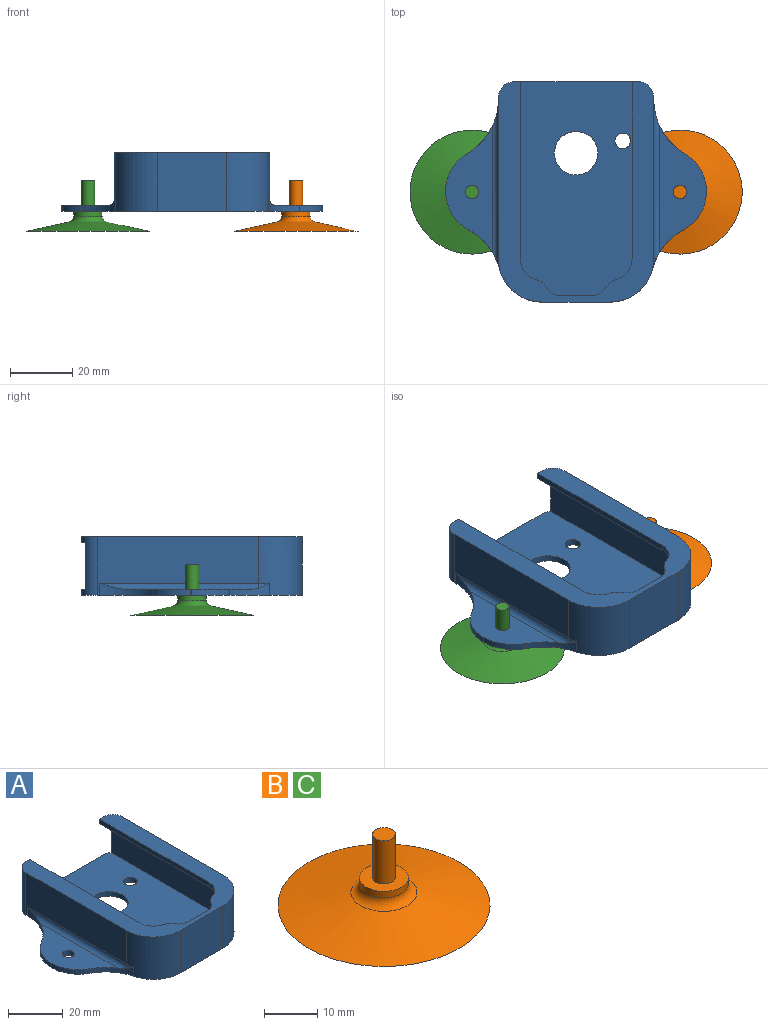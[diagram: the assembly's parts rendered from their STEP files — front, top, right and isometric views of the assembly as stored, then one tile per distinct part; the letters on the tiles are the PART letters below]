
ASSEMBLY  parts=3 mates=2
PART A: 48 faces, bbox 84.1x71x19 mm
  f0: plane 52x19mm, normal (-1,0,0), area 782.9mm2, adj f8,f9,f22,f27,f40,f43
  f1: plane 52x19mm, normal (1,0,0), area 782.9mm2, adj f8,f10,f22,f28,f33,f45
  f2: plane 40.1x2mm, normal (0,1,0), area 80.2mm2, adj f8,f14,f27,f28
  f3: plane 2x2mm, normal (0,1,0), area 4mm2, adj f5,f18,f22,f28
  f4: plane 69x18.01mm, normal (0,0,-1), area 367.1mm2, adj f6,f11,f12,f15,f20,f21,f23,f25
  f5: plane 69x18.01mm, normal (0,0,-1), area 367.1mm2, adj f3,f12,f13,f16,f18,f19,f24,f26
  f6: plane 2x2mm, normal (0,1,0), area 4mm2, adj f4,f21,f22,f27
  f7: plane 22.1x19mm, normal (0,-1,0), area 419.9mm2, adj f8,f9,f10,f22
  f8: plane 84.1x71mm, normal (0,0,-1), area 4177.7mm2, adj f0,f1,f2,f7,f9,f10,f17,f27
  f9: cylinder r=14mm len=19mm, axis (0,0,-1), area 403.8mm2, adj f0,f7,f8,f22,f39,f44
  f10: cylinder r=14mm len=19mm, axis (0,0,1), area 403.8mm2, adj f1,f7,f8,f22,f32,f46
  f11: plane 56x15mm, normal (1,0,0), area 840mm2, adj f4,f14,f15,f27
  f12: plane 22.1x17mm, normal (0,1,0), area 351.7mm2, adj f4,f5,f14,f15,f16,f22,f23,f24
  f13: plane 56x15mm, normal (-1,0,0), area 840mm2, adj f5,f14,f16,f28
  f14: plane 69x46.1mm, normal (0,0,1), area 2943.6mm2, adj f2,f11,f12,f13,f15,f16,f17,f27
  f15: cylinder r=12mm len=15mm, axis (0,0,-1), area 282.7mm2, adj f4,f11,f12,f14
  f16: cylinder r=12mm len=15mm, axis (0,0,1), area 282.7mm2, adj f5,f12,f13,f14
  f17: cylinder r=7mm len=14mm, axis (0,0,1), area 88mm2, adj f8,f14
  f18: plane 57x2mm, normal (-1,0,0), area 114mm2, adj f3,f5,f19,f22
  f19: cylinder r=7mm len=6.68mm, axis (0,0,-1), area 17.8mm2, adj f5,f18,f22,f26
  f20: cylinder r=7mm len=6.68mm, axis (0,0,-1), area 17.8mm2, adj f4,f21,f22,f25
  f21: plane 57x2mm, normal (1,0,0), area 114mm2, adj f4,f6,f20,f22
  f22: plane 71x50.1mm, normal (0,0,1), area 1079.3mm2, adj f0,f1,f3,f6,f7,f9,f10,f12
  f23: cylinder r=5mm len=4.24mm, axis (0,0,1), area 10.1mm2, adj f4,f12,f22,f25
  f24: cylinder r=5mm len=4.24mm, axis (0,0,1), area 10.1mm2, adj f5,f12,f22,f26
  f25: cylinder r=7mm len=3.85mm, axis (0,0,1), area 9.9mm2, adj f4,f20,f22,f23
  f26: cylinder r=7mm len=3.85mm, axis (0,0,1), area 9.9mm2, adj f5,f19,f22,f24
  f27: cylinder r=5mm len=19mm, axis (0,0,1), area 101mm2, adj f0,f2,f4,f6,f8,f11,f14,f22
  f28: cylinder r=5mm len=19mm, axis (0,0,-1), area 101mm2, adj f1,f2,f3,f5,f8,f13,f14,f22
  f29: plane 2x0.2mm, normal (1,0,0), area 0.4mm2, adj f8,f30,f34,f35
  f30: plane 40.34x15mm, normal (0,0,1), area 354.2mm2, adj f29,f31,f32,f33,f34,f35,f45
  f31: cylinder r=2.15mm len=4.3mm, axis (0,0,1), area 27mm2, adj f8,f30
  f32: cylinder r=20mm len=12.72mm, axis (0,0,1), area 38.1mm2, adj f8,f10,f30,f35,f45,f46
  f33: cylinder r=20mm len=17.32mm, axis (0,0,1), area 48.9mm2, adj f1,f8,f30,f34,f45
  f34: cylinder r=14mm len=12.12mm, axis (0,0,1), area 29.3mm2, adj f8,f29,f30,f33
  f35: cylinder r=14mm len=12.37mm, axis (0,0,1), area 30.3mm2, adj f8,f29,f30,f32
  f36: plane 2x0.2mm, normal (-1,0,0), area 0.4mm2, adj f8,f37,f41,f42
  f37: plane 40.34x15mm, normal (0,0,1), area 354.2mm2, adj f36,f38,f39,f40,f41,f42,f43
  f38: cylinder r=2.15mm len=4.3mm, axis (0,0,1), area 27mm2, adj f8,f37
  f39: cylinder r=20mm len=12.72mm, axis (0,0,1), area 38.1mm2, adj f8,f9,f37,f42,f43,f44
  f40: cylinder r=20mm len=17.32mm, axis (0,0,1), area 48.9mm2, adj f0,f8,f37,f41,f43
  f41: cylinder r=14mm len=12.12mm, axis (0,0,1), area 29.3mm2, adj f8,f36,f37,f40
  f42: cylinder r=14mm len=12.37mm, axis (0,0,1), area 30.3mm2, adj f8,f36,f37,f39
  f43: cylinder r=2mm len=51.27mm, axis (0,1,0), area 145mm2, adj f0,f37,f39,f40,f44
  f44: torus R=16mm, axis (0,0,-1), area 3.3mm2, adj f9,f39,f43
  f45: cylinder r=2mm len=51.27mm, axis (0,-1,0), area 145mm2, adj f1,f30,f32,f33,f46
  f46: torus R=16mm, axis (0,0,-1), area 3.3mm2, adj f10,f32,f45
  f47: cylinder r=2.5mm len=5mm, axis (0,0,1), area 31.4mm2, adj f8,f14
PART B: 7 faces, bbox 40x40x16.4 mm
  f0: plane 9.17x9.17mm, normal (0,0,1), area 51.5mm2, adj f1,f6
  f1: cylinder r=2.15mm len=10mm, axis (0,0,-1), area 135.1mm2, adj f0,f2
  f2: plane 4.3x4.3mm, normal (0,0,1), area 14.5mm2, adj f1
  f3: cone r=20mm half-angle=86.9deg, axis (0,0,-1), area 1258.5mm2, adj f4
  f4: cone r=6.23mm half-angle=77.7deg, axis (0,0,-1), area 1161.6mm2, adj f3,f5
  f5: torus R=6.58mm, axis (0,0,-1), area 90.4mm2, adj f4,f6
  f6: cylinder r=4.58mm len=9.17mm, axis (0,0,-1), area 42mm2, adj f0,f5
PART C: same geometry as B
PLACE A at identity
PLACE B t=(33.55,0,-19.11)mm
PLACE C t=(-33.55,0,-19.11)mm
MATE cylindrical B.f1 <-> A.f31  axis (0,0,1) through (33.55,0,-9.5)mm
MATE cylindrical C.f1 <-> A.f38  axis (0,0,1) through (-33.55,0,-9.5)mm
